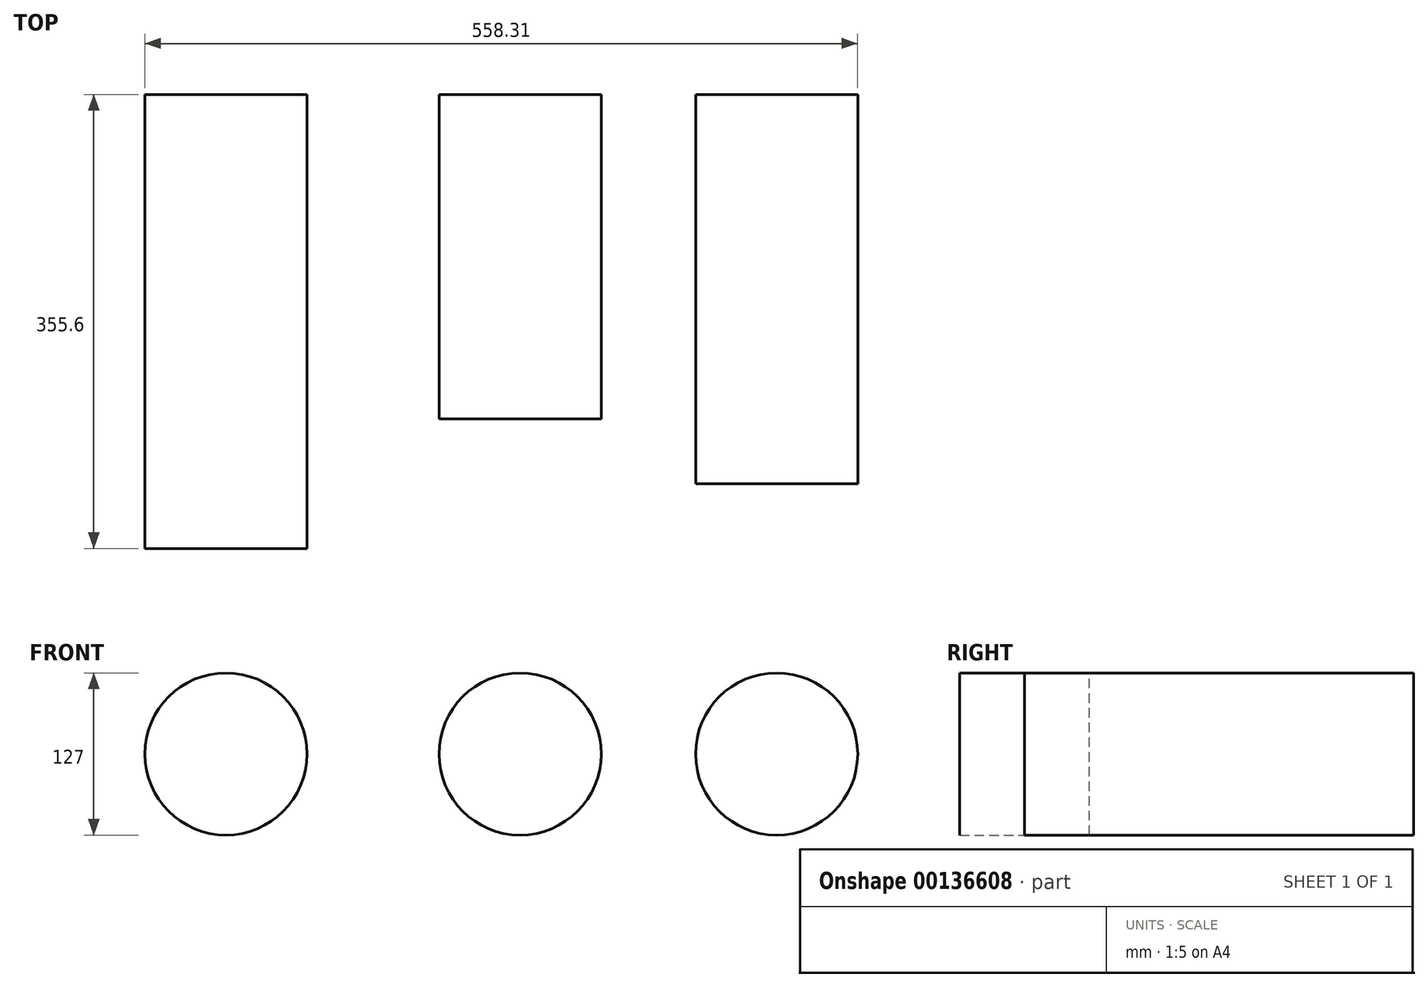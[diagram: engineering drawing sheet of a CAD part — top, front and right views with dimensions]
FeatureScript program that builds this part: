
annotation { "Feature Type Name" : "Feature", "Feature Type Description" : "" }
export const myFeature = defineFeature(function(context is Context, id is Id, definition is map)
    precondition{}
    {
        {
            var Q0;
            Q0=qCreatedBy(makeId("Front.planeOp"),FACE);
            var sketch = newSketch(context, id + "F0", { "sketchPlane" : qUnion([Q0])});
            skCircle(sketch, "E0", {"center": v(0, 0) * mm, "radius": 63.5 * mm});
            skSolve(sketch);
        }
        {
            var Q0;
            Q0=makeQuery(id+"F0.imprint","IMPRINT",FACE,{"disambiguationData":[TD([[makeQuery(id+"F0.imprint","IMPRINT",EDGE,{"derivedFrom":sQuery(id+"F0.wireOp",EDGE,"E0")}),1.0]])]});
            extrude(context, id + "F1", {"entities" : qUnion([Q0]), "depth" : 254 * mm});
        }
        {
            var Q0;
            Q0=qCreatedBy(makeId("Front.planeOp"),FACE);
            var sketch = newSketch(context, id + "F2", { "sketchPlane" : qUnion([Q0])});
            skCircle(sketch, "E1", {"center": v(200.91, 0) * mm, "radius": 63.5 * mm});
            skSolve(sketch);
        }
        {
            var Q0;
            Q0=makeQuery(id+"F2.imprint","IMPRINT",FACE,{"disambiguationData":[TD([[makeQuery(id+"F2.imprint","IMPRINT",EDGE,{"derivedFrom":sQuery(id+"F2.wireOp",EDGE,"E1")}),1.0]])]});
            extrude(context, id + "F3", {"entities" : qUnion([Q0]), "depth" : 304.8 * mm});
        }
        {
            var Q0;
            Q0=qCreatedBy(makeId("Front.planeOp"),FACE);
            var sketch = newSketch(context, id + "F4", { "sketchPlane" : qUnion([Q0])});
            skCircle(sketch, "E2", {"center": v(-230.4, 0) * mm, "radius": 63.5 * mm});
            skSolve(sketch);
        }
        {
            var Q0;
            Q0=makeQuery(id+"F4.imprint","IMPRINT",FACE,{"disambiguationData":[TD([[makeQuery(id+"F4.imprint","IMPRINT",EDGE,{"derivedFrom":sQuery(id+"F4.wireOp",EDGE,"E2")}),1.0]])]});
            extrude(context, id + "F5", {"entities" : qUnion([Q0]), "depth" : 355.6 * mm});
        }
    });
